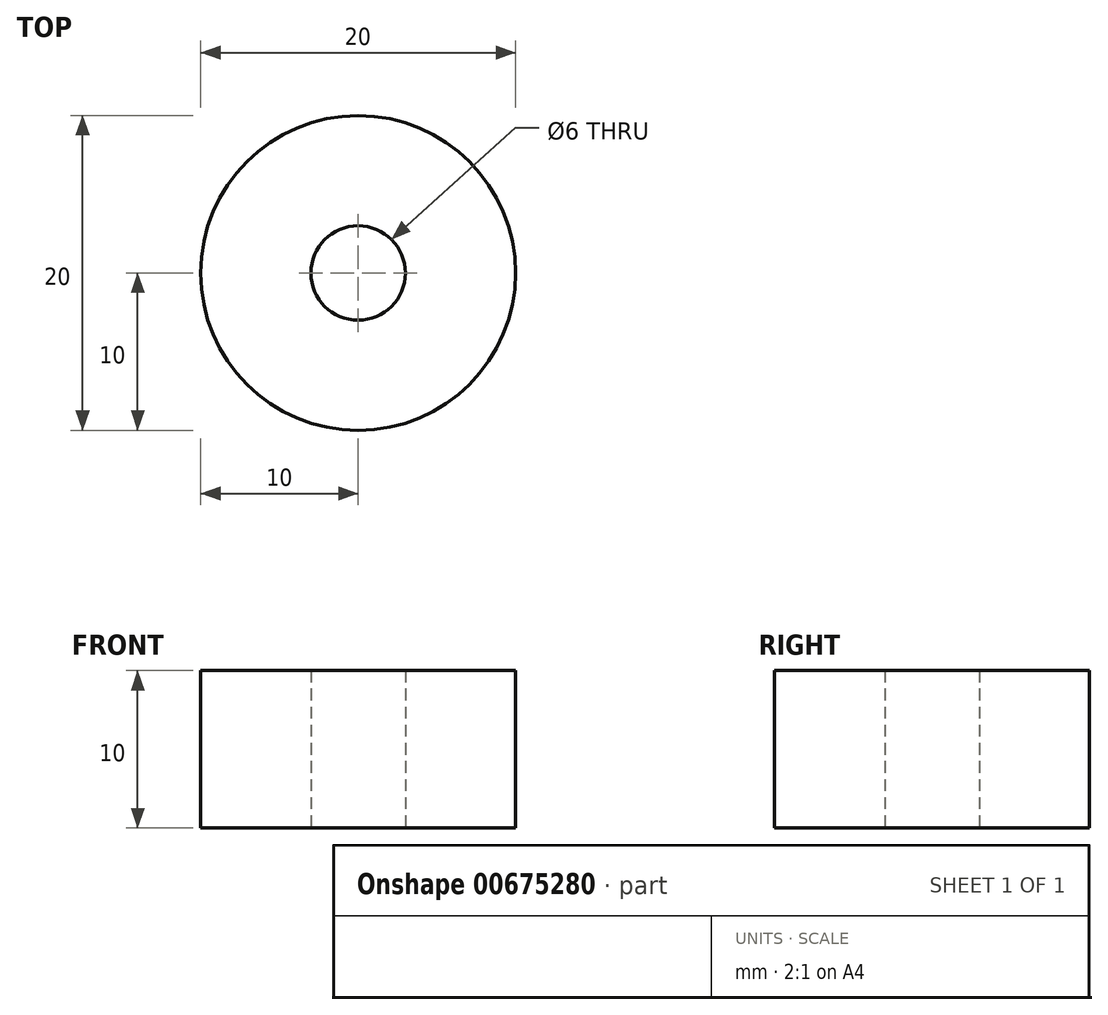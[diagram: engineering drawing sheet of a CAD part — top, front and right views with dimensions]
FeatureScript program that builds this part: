
annotation { "Feature Type Name" : "Feature", "Feature Type Description" : "" }
export const myFeature = defineFeature(function(context is Context, id is Id, definition is map)
    precondition{}
    {
        {
            var Q0;
            Q0=qCreatedBy(makeId("Top.planeOp"),FACE);
            var sketch = newSketch(context, id + "F0", { "sketchPlane" : qUnion([Q0])});
            skCircle(sketch, "E0", {"center": v(0, 0) * mm, "radius": 3 * mm});
            skCircle(sketch, "E1", {"center": v(0, 0) * mm, "radius": 10 * mm});
            skSolve(sketch);
        }
        {
            var Q0;
            Q0=qSketchRegion(id+"F0",true);
            extrude(context, id + "F1", {"entities" : qUnion([Q0]), "depth" : 10 * mm, "offsetDistance" : 25 * mm});
        }
    });
